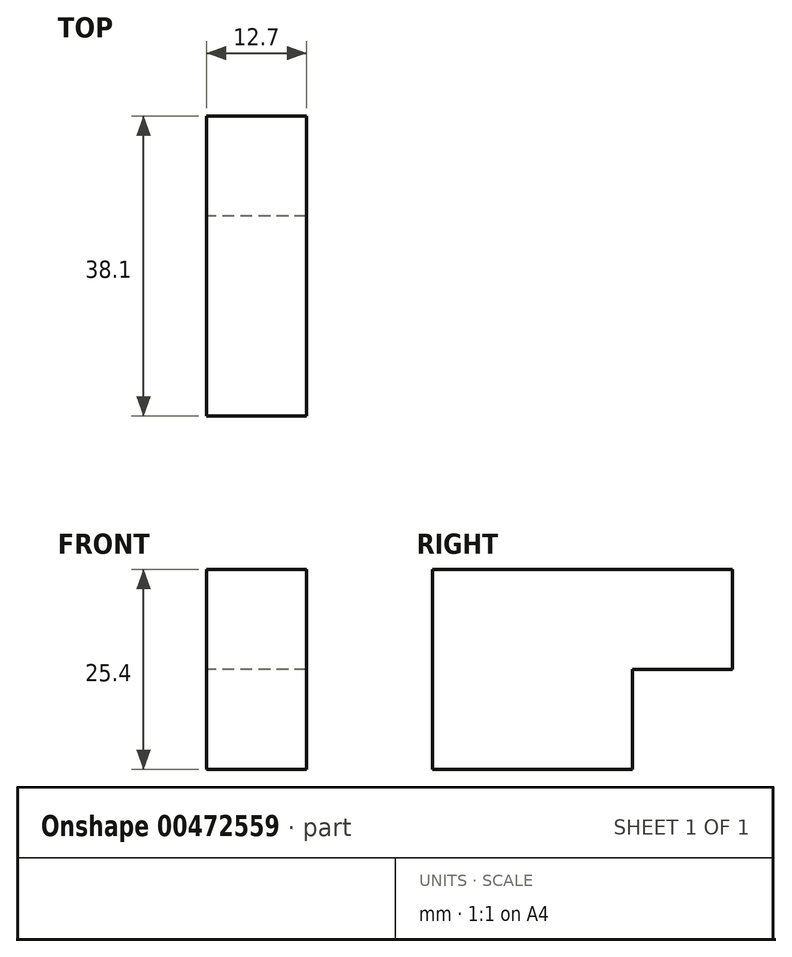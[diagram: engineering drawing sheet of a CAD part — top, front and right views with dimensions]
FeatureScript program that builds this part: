
annotation { "Feature Type Name" : "Feature", "Feature Type Description" : "" }
export const myFeature = defineFeature(function(context is Context, id is Id, definition is map)
    precondition{}
    {
        {
            var Q0;
            Q0=qCreatedBy(makeId("Right.planeOp"),FACE);
            var sketch = newSketch(context, id + "F0", { "sketchPlane" : qUnion([Q0])});
            skLineSegment(sketch, "E0", {"start": v(-25.4, 0) * mm, "end": v(-25.4, 25.4) * mm});
            skLineSegment(sketch, "E1", {"start": v(-25.4, 25.4) * mm, "end": v(12.7, 25.4) * mm});
            skLineSegment(sketch, "E2", {"start": v(12.7, 12.7) * mm, "end": v(0, 12.7) * mm});
            skLineSegment(sketch, "E3", {"start": v(0, 12.7) * mm, "end": v(0, 0) * mm});
            skLineSegment(sketch, "E4", {"start": v(12.7, 12.7) * mm, "end": v(12.7, 25.4) * mm});
            skLineSegment(sketch, "E5", {"start": v(-25.4, 0) * mm, "end": v(0, 0) * mm});
            skSolve(sketch);
        }
        {
            var Q0;
            Q0 = qSketchRegion(id + "F0", true);
            extrude(context, id + "F1", {"entities" : qUnion([Q0]), "depth" : 12.7 * mm});
        }
    });
